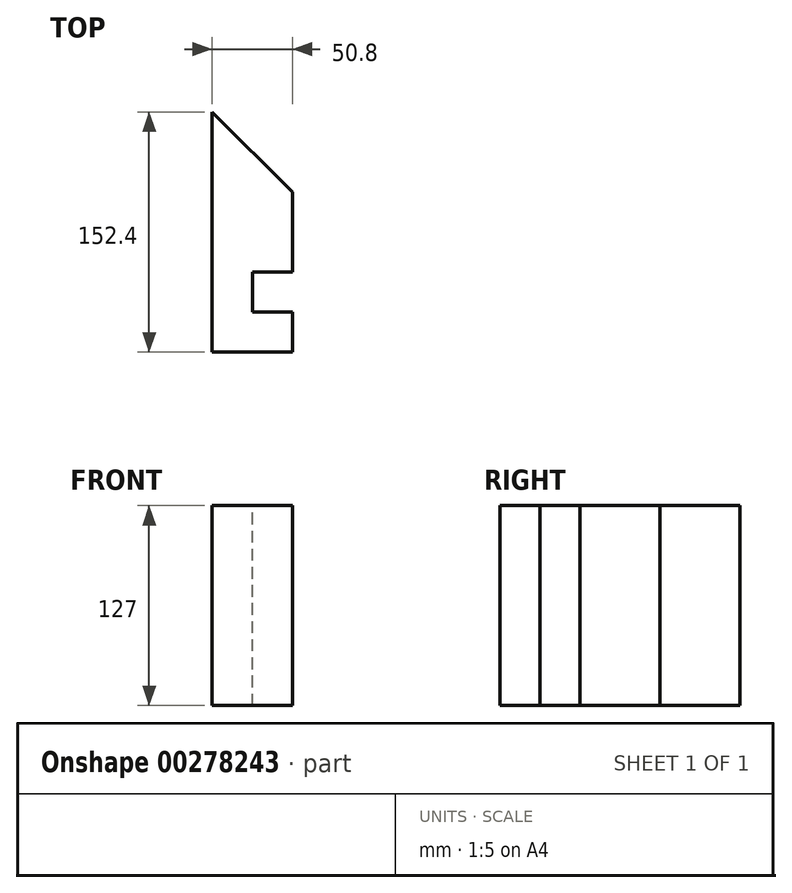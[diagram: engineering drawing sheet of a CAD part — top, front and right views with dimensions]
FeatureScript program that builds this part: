
annotation { "Feature Type Name" : "Feature", "Feature Type Description" : "" }
export const myFeature = defineFeature(function(context is Context, id is Id, definition is map)
    precondition{}
    {
        {
            var Q0;
            Q0=qCreatedBy(makeId("Top.planeOp"),FACE);
            var sketch = newSketch(context, id + "F0", { "sketchPlane" : qUnion([Q0])});
            skLineSegment(sketch, "E0", {"start": v(0, 0) * mm, "end": v(50.8, 0) * mm});
            skLineSegment(sketch, "E1", {"start": v(0, 0) * mm, "end": v(0, 152.4) * mm});
            skLineSegment(sketch, "E2", {"start": v(50.8, 0) * mm, "end": v(50.8, 25.4) * mm});
            skLineSegment(sketch, "E3", {"start": v(50.8, 25.4) * mm, "end": v(25.4, 25.4) * mm});
            skLineSegment(sketch, "E4", {"start": v(25.4, 25.4) * mm, "end": v(25.4, 50.8) * mm});
            skLineSegment(sketch, "E5", {"start": v(25.4, 50.8) * mm, "end": v(50.8, 50.8) * mm});
            skLineSegment(sketch, "E6", {"start": v(50.8, 50.8) * mm, "end": v(50.8, 101.6) * mm});
            skLineSegment(sketch, "E7", {"start": v(0, 152.4) * mm, "end": v(50.8, 101.6) * mm});
            skSolve(sketch);
        }
        {
            var Q0;
            Q0=qCreatedBy(makeId("Right.planeOp"),FACE);
            var sketch = newSketch(context, id + "F1", { "sketchPlane" : qUnion([Q0])});
            skLineSegment(sketch, "E8", {"start": v(0, 0) * mm, "end": v(0, 127) * mm});
            skSolve(sketch);
        }
        {
            var Q0;
            Q0=makeQuery(id+"F0.imprint","IMPRINT",FACE,{"disambiguationData":[TD([[makeQuery(id+"F0.imprint","IMPRINT",EDGE,{"derivedFrom":sQuery(id+"F0.wireOp",EDGE,"E0")}),1.0]])]});
            var Q1;
            Q1=sQuery(id+"F1.wireOp",EDGE,"E8");
            sweep(context, id + "F2", {"profiles" : qUnion([Q0]), "path" : qUnion([Q1])});
        }
    });
